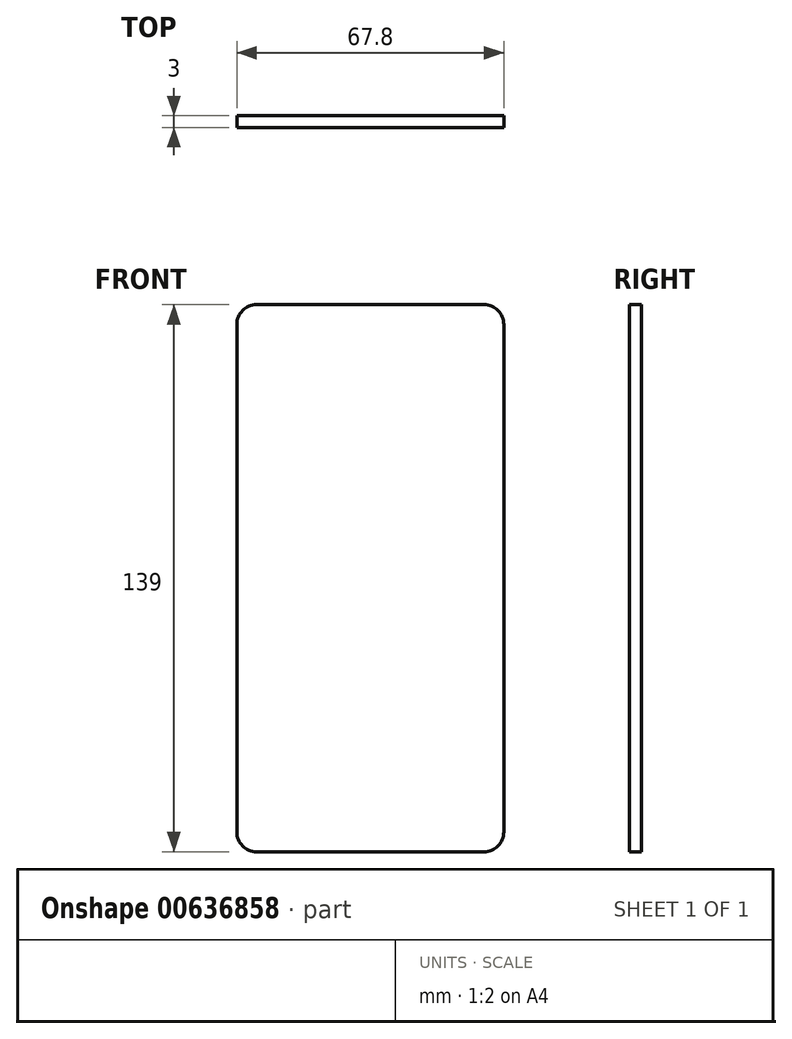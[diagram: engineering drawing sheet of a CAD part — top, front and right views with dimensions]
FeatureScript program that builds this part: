
annotation { "Feature Type Name" : "Feature", "Feature Type Description" : "" }
export const myFeature = defineFeature(function(context is Context, id is Id, definition is map)
    precondition{}
    {
        {
            var Q0;
            Q0=qCreatedBy(makeId("Front.planeOp"),FACE);
            var sketch = newSketch(context, id + "F0", { "sketchPlane" : qUnion([Q0])});
            skLineSegment(sketch, "E0", {"start": v(0, -63.47) * mm, "end": v(0, 75.53) * mm});
            skLineSegment(sketch, "E1", {"start": v(67.8, 75.53) * mm, "end": v(0, 75.53) * mm});
            skLineSegment(sketch, "E2", {"start": v(67.8, 75.53) * mm, "end": v(67.8, -63.47) * mm});
            skLineSegment(sketch, "E3", {"start": v(67.8, -63.47) * mm, "end": v(0, -63.47) * mm});
            skSolve(sketch);
        }
        {
            var Q0;
            Q0 = qSketchRegion(id + "F0", true);
            extrude(context, id + "F1", {"entities" : qUnion([Q0]), "depth" : 3 * mm, "offsetDistance" : 25 * mm});
        }
        {
            var Q0;
            Q0=makeQuery(id+"F1.opExtrude","SWEPT_EDGE",EDGE,{"disambiguationData":[OSD([sQuery(id+"F0.wireOp",EDGE,"E1"),sQuery(id+"F0.wireOp",EDGE,"E2")])]});
            var Q1;
            Q1=makeQuery(id+"F1.opExtrude","SWEPT_EDGE",EDGE,{"disambiguationData":[OSD([sQuery(id+"F0.wireOp",EDGE,"E0"),sQuery(id+"F0.wireOp",EDGE,"E1")])]});
            var Q2;
            Q2=makeQuery(id+"F1.opExtrude","SWEPT_EDGE",EDGE,{"disambiguationData":[OSD([sQuery(id+"F0.wireOp",EDGE,"E0"),sQuery(id+"F0.wireOp",EDGE,"E3")])]});
            var Q3;
            Q3=makeQuery(id+"F1.opExtrude","SWEPT_EDGE",EDGE,{"disambiguationData":[OSD([sQuery(id+"F0.wireOp",EDGE,"E2"),sQuery(id+"F0.wireOp",EDGE,"E3")])]});
            fillet(context, id + "F2", {"entities" : qUnion([Q0, Q1, Q2, Q3]), "radius" : 5 * mm, "tangentPropagation" : true, "allowEdgeOverflow" : false});
        }
    });
